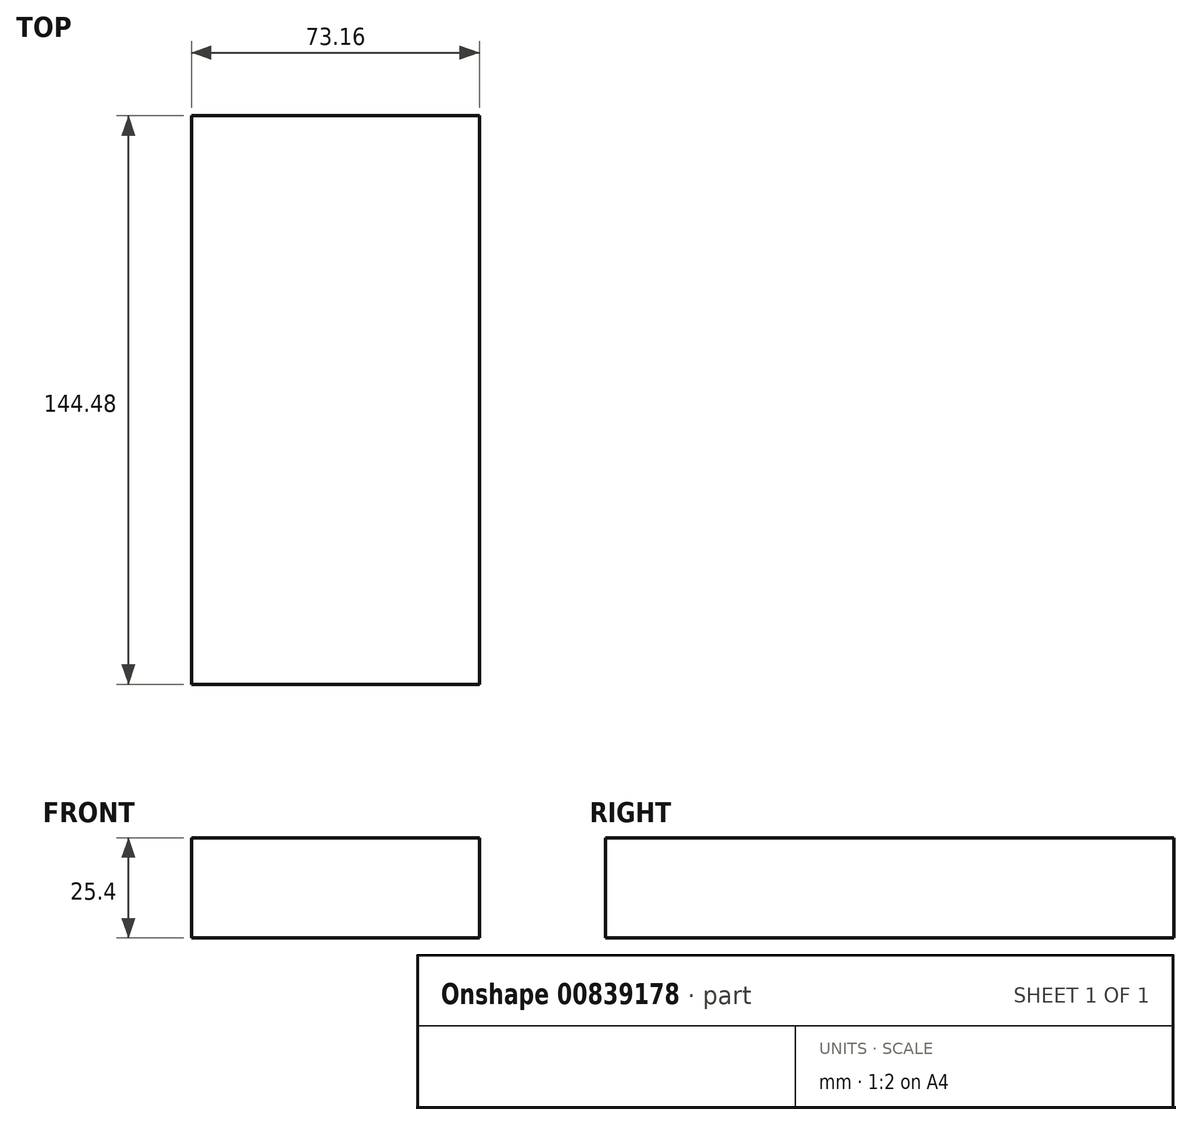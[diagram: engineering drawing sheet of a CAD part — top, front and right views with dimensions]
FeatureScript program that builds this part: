
annotation { "Feature Type Name" : "Feature", "Feature Type Description" : "" }
export const myFeature = defineFeature(function(context is Context, id is Id, definition is map)
    precondition{}
    {
        {
            var Q0;
            Q0=qCreatedBy(makeId("Top.planeOp"),FACE);
            var sketch = newSketch(context, id + "F0", { "sketchPlane" : qUnion([Q0])});
            skLineSegment(sketch, "E0.bottom", {"start": v(73.16, 103.56) * mm, "end": v(0, 103.56) * mm});
            skLineSegment(sketch, "E0.top", {"start": v(73.16, 248.04) * mm, "end": v(0, 248.04) * mm});
            skLineSegment(sketch, "E0.left", {"start": v(73.16, 103.56) * mm, "end": v(73.16, 248.04) * mm});
            skLineSegment(sketch, "E0.right", {"start": v(0, 103.56) * mm, "end": v(0, 248.04) * mm});
            skSolve(sketch);
        }
        {
            var Q0;
            Q0 = qSketchRegion(id + "F0", true);
            extrude(context, id + "F1", {"entities" : qUnion([Q0]), "depth" : 25.4 * mm, "offsetDistance" : 25.4 * mm});
        }
    });
